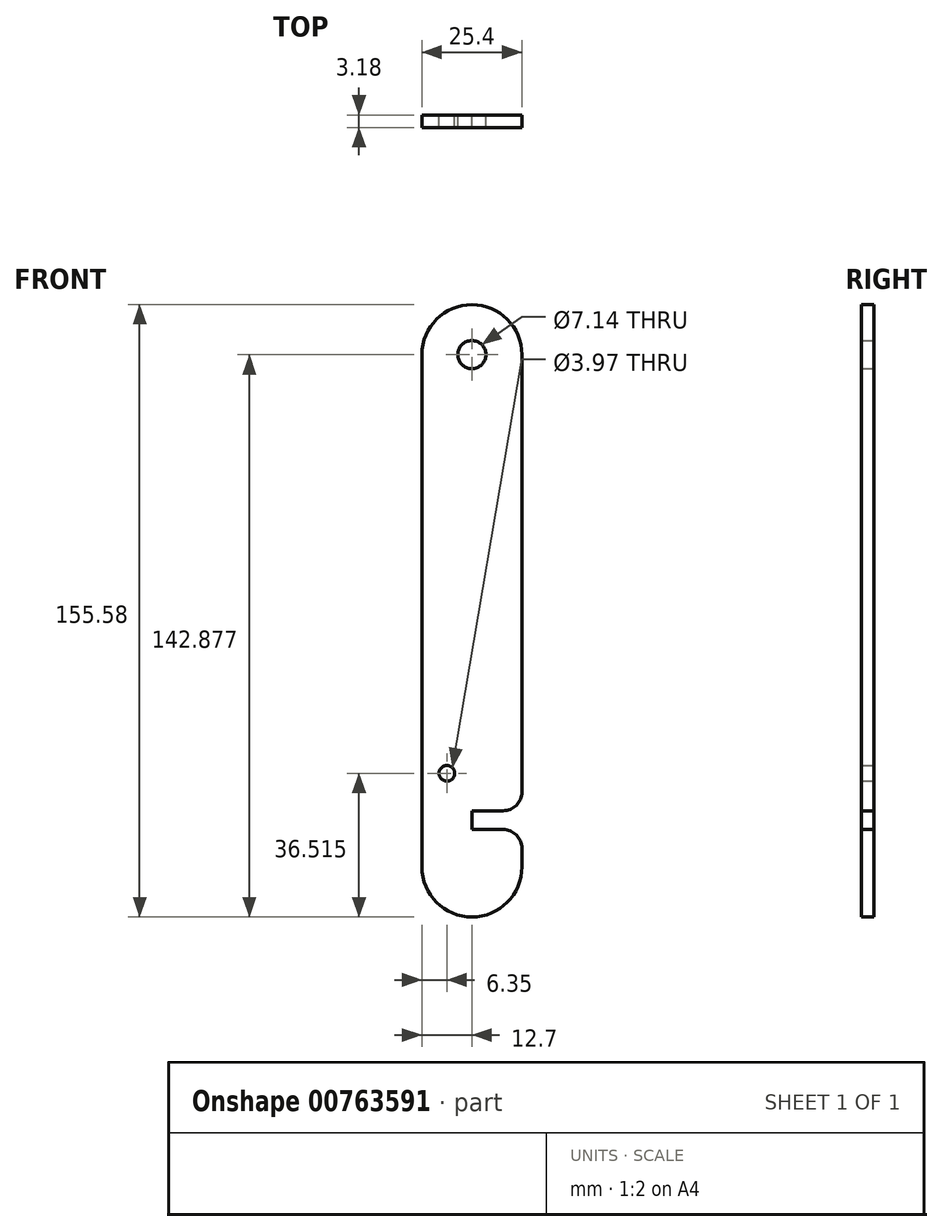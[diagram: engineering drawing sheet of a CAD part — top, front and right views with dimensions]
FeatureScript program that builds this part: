
annotation { "Feature Type Name" : "Feature", "Feature Type Description" : "" }
export const myFeature = defineFeature(function(context is Context, id is Id, definition is map)
    precondition{}
    {
        {
            var Q0;
            Q0=qCreatedBy(makeId("Front.planeOp"),FACE);
            var sketch = newSketch(context, id + "F0", { "sketchPlane" : qUnion([Q0])});
            skLineSegment(sketch, "E0", {"start": v(0, 65.09) * mm, "end": v(0, -65.09) * mm, "construction": true});
            skArc(sketch, "E1", {"start": v(12.7, 65.09) * mm, "mid": v(0, 77.79) * mm, "end": v(-12.7, 65.09) * mm});
            skArc(sketch, "E2", {"start": v(-12.7, -65.09) * mm, "mid": v(0, -77.79) * mm, "end": v(12.7, -65.09) * mm});
            skLineSegment(sketch, "E3", {"start": v(-12.7, 65.09) * mm, "end": v(-12.7, -65.09) * mm});
            skLineSegment(sketch, "E4", {"start": v(12.7, 65.09) * mm, "end": v(12.7, -50.8) * mm});
            skLineSegment(sketch, "E5", {"start": v(12.7, -55.56) * mm, "end": v(0, -55.56) * mm});
            skLineSegment(sketch, "E6", {"start": v(0, -55.56) * mm, "end": v(0, -50.8) * mm});
            skLineSegment(sketch, "E7", {"start": v(0, -50.8) * mm, "end": v(12.7, -50.8) * mm});
            skLineSegment(sketch, "E8.trimOffspring", {"start": v(12.7, -55.56) * mm, "end": v(12.7, -65.09) * mm});
            skSolve(sketch);
        }
        {
            var Q0;
            Q0=makeQuery(id+"F0.imprint","IMPRINT",FACE,{"disambiguationData":[TD([[makeQuery(id+"F0.imprint","IMPRINT",EDGE,{"derivedFrom":sQuery(id+"F0.wireOp",EDGE,"E1")}),1.0]])]});
            extrude(context, id + "F1", {"entities" : qUnion([Q0]), "depth" : 3.17 * mm, "offsetDistance" : 25.4 * mm});
        }
        {
            var Q0;
            Q0=makeQuery(id+"F1.opExtrude","CAP_FACE",FACE,{"disambiguationData":[OSD([sQuery(id+"F0.wireOp",EDGE,"E1"),sQuery(id+"F0.wireOp",EDGE,"E2"),sQuery(id+"F0.wireOp",EDGE,"E3"),sQuery(id+"F0.wireOp",EDGE,"E4"),sQuery(id+"F0.wireOp",EDGE,"E5"),sQuery(id+"F0.wireOp",EDGE,"E6"),sQuery(id+"F0.wireOp",EDGE,"E7"),sQuery(id+"F0.wireOp",EDGE,"E8.trimOffspring")])],"isStart":false});
            var sketch = newSketch(context, id + "F2", { "sketchPlane" : qUnion([Q0])});
            skPoint(sketch, "E9", {"position": v(0, 65.09) * mm});
            skSolve(sketch);
        }
        {
            var Q0;
            Q0=sQuery(id+"F2.wireOp",VERTEX,"E9");
            var Q1;
            Q1=makeQuery(id+"F1.opExtrude","SWEPT_BODY",BODY,{"disambiguationData":[OSD([sQuery(id+"F0.wireOp",EDGE,"E1"),sQuery(id+"F0.wireOp",EDGE,"E2"),sQuery(id+"F0.wireOp",EDGE,"E3"),sQuery(id+"F0.wireOp",EDGE,"E4"),sQuery(id+"F0.wireOp",EDGE,"E5"),sQuery(id+"F0.wireOp",EDGE,"E6"),sQuery(id+"F0.wireOp",EDGE,"E7"),sQuery(id+"F0.wireOp",EDGE,"E8.trimOffspring")])]});
            hole(context, id + "F3", {"style" : HoleStyle.SIMPLE, "endStyle" : HoleEndStyle.THROUGH, "holeDiameter" : 7.14 * mm, "majorDiameter" : 6.35 * mm, "isTappedThrough" : true, "tappedDepth" : 12.7 * mm, "tapClearance" : 3, "locations" : qUnion([Q0]), "scope" : qUnion([Q1]), "startStyle" : HoleStartStyle.PART});
        }
        {
            var Q0;
            Q0=makeQuery(id+"F1.opExtrude","CAP_FACE",FACE,{"disambiguationData":[OSD([sQuery(id+"F0.wireOp",EDGE,"E1"),sQuery(id+"F0.wireOp",EDGE,"E2"),sQuery(id+"F0.wireOp",EDGE,"E3"),sQuery(id+"F0.wireOp",EDGE,"E4"),sQuery(id+"F0.wireOp",EDGE,"E5"),sQuery(id+"F0.wireOp",EDGE,"E6"),sQuery(id+"F0.wireOp",EDGE,"E7"),sQuery(id+"F0.wireOp",EDGE,"E8.trimOffspring")])],"isStart":false});
            var sketch = newSketch(context, id + "F4", { "sketchPlane" : qUnion([Q0])});
            skLineSegment(sketch, "E10", {"start": v(-12.7, -41.28) * mm, "end": v(-6.35, -41.28) * mm, "construction": true});
            skPoint(sketch, "E11", {"position": v(-6.35, -41.28) * mm});
            skSolve(sketch);
        }
        {
            var Q0;
            Q0=sQuery(id+"F4.wireOp",VERTEX,"E11");
            var Q1;
            Q1=makeQuery(id+"F1.opExtrude","SWEPT_BODY",BODY,{"disambiguationData":[OSD([sQuery(id+"F0.wireOp",EDGE,"E1"),sQuery(id+"F0.wireOp",EDGE,"E2"),sQuery(id+"F0.wireOp",EDGE,"E3"),sQuery(id+"F0.wireOp",EDGE,"E4"),sQuery(id+"F0.wireOp",EDGE,"E5"),sQuery(id+"F0.wireOp",EDGE,"E6"),sQuery(id+"F0.wireOp",EDGE,"E7"),sQuery(id+"F0.wireOp",EDGE,"E8.trimOffspring")])]});
            hole(context, id + "F5", {"style" : HoleStyle.SIMPLE, "endStyle" : HoleEndStyle.THROUGH, "holeDiameter" : 3.97 * mm, "majorDiameter" : 6.35 * mm, "isTappedThrough" : true, "tappedDepth" : 12.7 * mm, "tapClearance" : 3, "locations" : qUnion([Q0]), "scope" : qUnion([Q1]), "startStyle" : HoleStartStyle.PART});
        }
        {
            var Q0;
            Q0=makeQuery(id+"F1.opExtrude","SWEPT_EDGE",EDGE,{"disambiguationData":[OSD([sQuery(id+"F0.wireOp",EDGE,"E5"),sQuery(id+"F0.wireOp",EDGE,"E8.trimOffspring")])]});
            var Q1;
            Q1=makeQuery(id+"F1.opExtrude","SWEPT_EDGE",EDGE,{"disambiguationData":[OSD([sQuery(id+"F0.wireOp",EDGE,"E4"),sQuery(id+"F0.wireOp",EDGE,"E7")])]});
            fillet(context, id + "F6", {"entities" : qUnion([Q0, Q1]), "tangentPropagation" : true, "radius" : 4.78 * mm, "defaultsChanged" : true, "vertexSettings" : [], "allowEdgeOverflow" : false});
        }
    });
